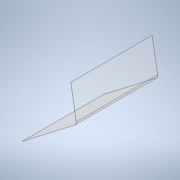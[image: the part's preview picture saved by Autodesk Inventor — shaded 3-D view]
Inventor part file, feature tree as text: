
AUTODESK INVENTOR PART (.ipt)
format: ipt  version: 2020.2 (Build 242310000, 310)  size: 106,496 bytes
history: native  units: mm
features: other x1, extrude x1, sketch x1
ambient origin geometry x8: Origin, YZ Plane, XZ Plane, XY Plane, X Axis, Y Axis, Z Axis, Center Point
bodies: Body1 (feature_tree)
feature tree (3):
  other  "ソリッド1"
  extrude  "押し出し1"  Depth=0.5mm
  sketch  "スケッチ1"
